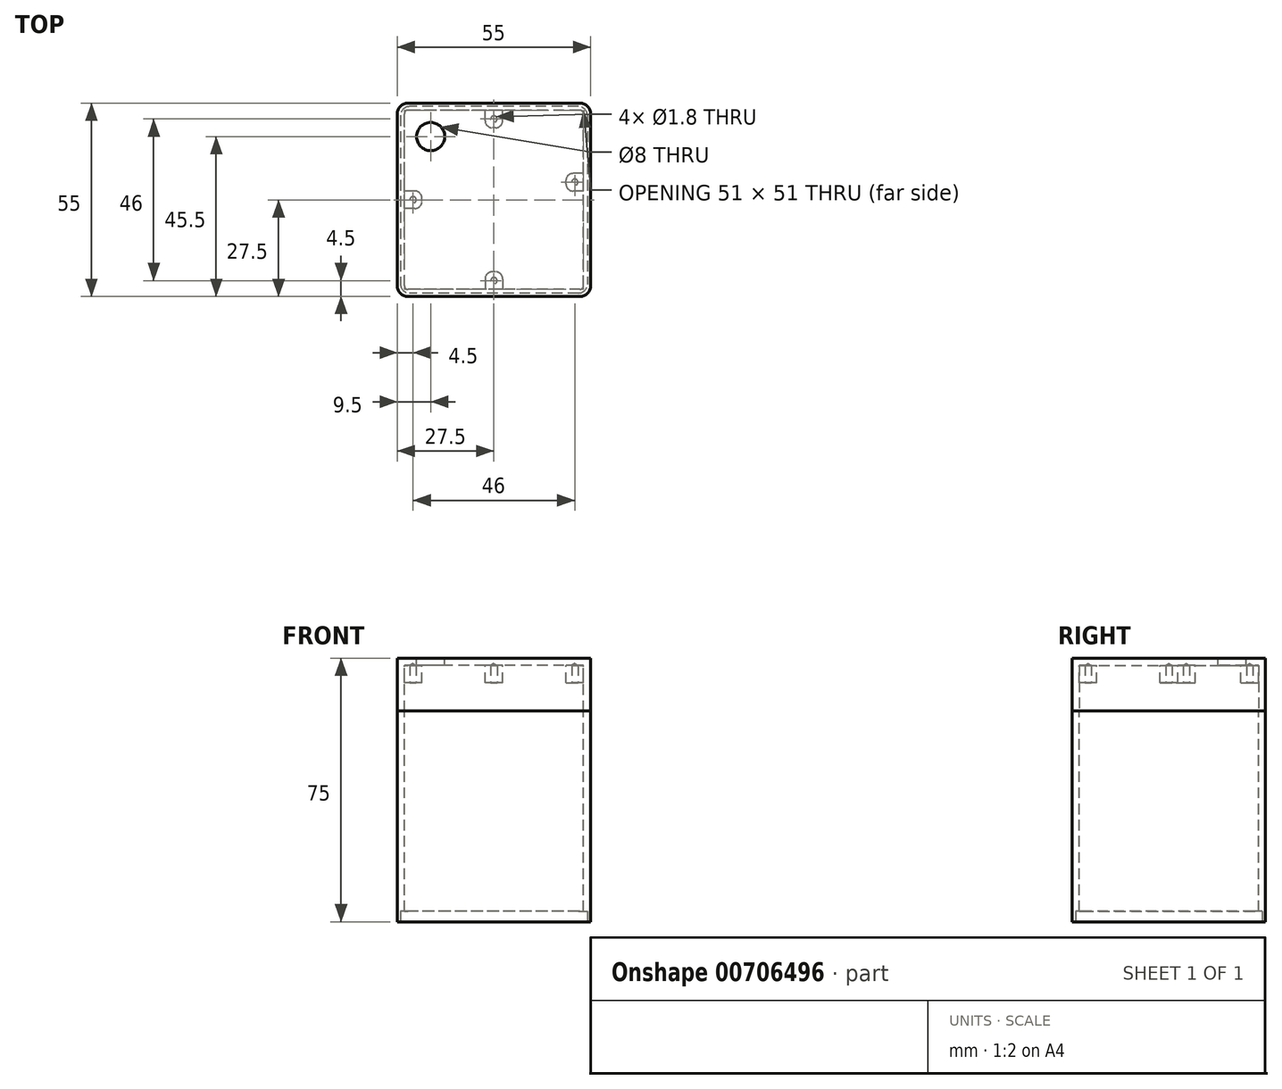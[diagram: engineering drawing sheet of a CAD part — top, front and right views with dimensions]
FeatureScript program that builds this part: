
annotation { "Feature Type Name" : "Feature", "Feature Type Description" : "" }
export const myFeature = defineFeature(function(context is Context, id is Id, definition is map)
    precondition{}
    {
        {
            var Q0;
            Q0=qCreatedBy(makeId("Top.planeOp"),FACE);
            var sketch = newSketch(context, id + "F0", { "sketchPlane" : qUnion([Q0])});
            skLineSegment(sketch, "E0.bottom", {"start": v(27.5, -27.5) * mm, "end": v(-27.5, -27.5) * mm});
            skLineSegment(sketch, "E0.top", {"start": v(27.5, 27.5) * mm, "end": v(-27.5, 27.5) * mm});
            skLineSegment(sketch, "E0.left", {"start": v(27.5, -27.5) * mm, "end": v(27.5, 27.5) * mm});
            skLineSegment(sketch, "E0.right", {"start": v(-27.5, -27.5) * mm, "end": v(-27.5, 27.5) * mm});
            skPoint(sketch, "E0.middle", {"position": v(0, 0) * mm});
            skSolve(sketch);
        }
        {
            var Q0;
            Q0=makeQuery(id+"F0.imprint","IMPRINT",FACE,{"disambiguationData":[TD([[makeQuery(id+"F0.imprint","IMPRINT",EDGE,{"derivedFrom":sQuery(id+"F0.wireOp",EDGE,"E0.bottom")}),-1.0]])]});
            extrude(context, id + "F1", {"entities" : qUnion([Q0]), "depth" : 15 * mm, "offsetDistance" : 25 * mm});
        }
        {
            var Q0;
            Q0=makeQuery(id+"F1.opExtrude","SWEPT_EDGE",EDGE,{"disambiguationData":[OSD([sQuery(id+"F0.wireOp",EDGE,"E0.top"),sQuery(id+"F0.wireOp",EDGE,"E0.right")])]});
            var Q1;
            Q1=makeQuery(id+"F1.opExtrude","SWEPT_EDGE",EDGE,{"disambiguationData":[OSD([sQuery(id+"F0.wireOp",EDGE,"E0.bottom"),sQuery(id+"F0.wireOp",EDGE,"E0.right")])]});
            var Q2;
            Q2=makeQuery(id+"F1.opExtrude","SWEPT_EDGE",EDGE,{"disambiguationData":[OSD([sQuery(id+"F0.wireOp",EDGE,"E0.bottom"),sQuery(id+"F0.wireOp",EDGE,"E0.left")])]});
            var Q3;
            Q3=makeQuery(id+"F1.opExtrude","SWEPT_EDGE",EDGE,{"disambiguationData":[OSD([sQuery(id+"F0.wireOp",EDGE,"E0.top"),sQuery(id+"F0.wireOp",EDGE,"E0.left")])]});
            fillet(context, id + "F2", {"entities" : qUnion([Q0, Q1, Q2, Q3]), "radius" : 3 * mm, "tangentPropagation" : true, "allowEdgeOverflow" : false});
        }
        {
            var Q0;
            Q0=makeQuery(id+"F1.opExtrude","CAP_FACE",FACE,{"disambiguationData":[OSD([sQuery(id+"F0.wireOp",EDGE,"E0.bottom"),sQuery(id+"F0.wireOp",EDGE,"E0.top"),sQuery(id+"F0.wireOp",EDGE,"E0.left"),sQuery(id+"F0.wireOp",EDGE,"E0.right")])],"isStart":true});
            shell(context, id + "F3", {"entities" : qUnion([Q0]), "thickness" : 2 * mm});
        }
        {
            var Q0;
            Q0=makeQuery(id+"F1.opExtrude","CAP_FACE",FACE,{"disambiguationData":[OSD([sQuery(id+"F0.wireOp",EDGE,"E0.bottom"),sQuery(id+"F0.wireOp",EDGE,"E0.top"),sQuery(id+"F0.wireOp",EDGE,"E0.left"),sQuery(id+"F0.wireOp",EDGE,"E0.right")])],"isStart":false});
            var sketch = newSketch(context, id + "F4", { "sketchPlane" : qUnion([Q0])});
            skCircle(sketch, "E1", {"center": v(-18, 18) * mm, "radius": 4 * mm});
            skLineSegment(sketch, "E2", {"start": v(-18, 18) * mm, "end": v(-18, 32.81) * mm, "construction": true});
            skSolve(sketch);
        }
        {
            var Q0;
            Q0=makeQuery(id+"F4.imprint","IMPRINT",FACE,{"disambiguationData":[TD([[makeQuery(id+"F4.imprint","IMPRINT",EDGE,{"derivedFrom":sQuery(id+"F4.wireOp",EDGE,"E1")}),1.0]])]});
            extrude(context, id + "F5", {"entities" : qUnion([Q0]), "operationType" : NewBodyOperationType.REMOVE, "oppositeDirection" : true, "depth" : 25 * mm, "offsetDistance" : 25 * mm});
        }
        {
            var Q0;
            Q0=makeQuery(id+"F1.opExtrude","CAP_FACE",FACE,{"disambiguationData":[OSD([sQuery(id+"F0.wireOp",EDGE,"E0.bottom"),sQuery(id+"F0.wireOp",EDGE,"E0.top"),sQuery(id+"F0.wireOp",EDGE,"E0.left"),sQuery(id+"F0.wireOp",EDGE,"E0.right")])],"isStart":true});
            extrude(context, id + "F6", {"entities" : qUnion([Q0]), "depth" : 60 * mm, "offsetDistance" : 25 * mm});
        }
        {
            var Q0;
            Q0=makeQuery(id+"F6.opExtrude","CAP_FACE",FACE,{"disambiguationData":[OSD([sQuery(id+"F0.wireOp",EDGE,"E0.bottom"),sQuery(id+"F0.wireOp",EDGE,"E0.top"),sQuery(id+"F0.wireOp",EDGE,"E0.left"),sQuery(id+"F0.wireOp",EDGE,"E0.right")])],"isStart":false});
            var sketch = newSketch(context, id + "F7", { "sketchPlane" : qUnion([Q0])});
            skLineSegment(sketch, "E3.bottom", {"start": v(24.05, -26.55) * mm, "end": v(-24.05, -26.55) * mm});
            skLineSegment(sketch, "E3.top", {"start": v(24.05, 26.55) * mm, "end": v(-24.05, 26.55) * mm});
            skLineSegment(sketch, "E3.left", {"start": v(26.55, -24.05) * mm, "end": v(26.55, 24.05) * mm});
            skLineSegment(sketch, "E3.right", {"start": v(-26.55, -24.05) * mm, "end": v(-26.55, 24.05) * mm});
            skPoint(sketch, "E3.middle", {"position": v(0, 0) * mm});
            skPoint(sketch, "E4.visualSharp", {"position": v(-26.55, -26.55) * mm});
            skArc(sketch, "E4.filletArc", {"start": v(-26.55, -24.05) * mm, "mid": v(-25.82, -25.82) * mm, "end": v(-24.05, -26.55) * mm});
            skPoint(sketch, "E5.visualSharp", {"position": v(26.55, -26.55) * mm});
            skArc(sketch, "E5.filletArc", {"start": v(24.05, -26.55) * mm, "mid": v(25.82, -25.82) * mm, "end": v(26.55, -24.05) * mm});
            skPoint(sketch, "E6.visualSharp", {"position": v(26.55, 26.55) * mm});
            skArc(sketch, "E6.filletArc", {"start": v(26.55, 24.05) * mm, "mid": v(25.82, 25.82) * mm, "end": v(24.05, 26.55) * mm});
            skPoint(sketch, "E7.visualSharp", {"position": v(-26.55, 26.55) * mm});
            skArc(sketch, "E7.filletArc", {"start": v(-24.05, 26.55) * mm, "mid": v(-25.82, 25.82) * mm, "end": v(-26.55, 24.05) * mm});
            skSolve(sketch);
        }
        {
            var Q0;
            Q0 = qSketchRegion(id + "F7", true);
            extrude(context, id + "F8", {"entities" : qUnion([Q0]), "operationType" : NewBodyOperationType.REMOVE, "oppositeDirection" : true, "depth" : 3 * mm, "offsetDistance" : 25 * mm});
        }
        {
            var Q0;
            Q0=makeQuery(id+"F3.opShell","OFFSET_FACE",FACE,{"disambiguationData":[OSD([sQuery(id+"F0.wireOp",EDGE,"E0.bottom"),sQuery(id+"F0.wireOp",EDGE,"E0.top"),sQuery(id+"F0.wireOp",EDGE,"E0.left"),sQuery(id+"F0.wireOp",EDGE,"E0.right")])]});
            var sketch = newSketch(context, id + "F9", { "sketchPlane" : qUnion([Q0])});
            skLineSegment(sketch, "E8.bottom", {"start": v(-20.5, 2.5) * mm, "end": v(-25.5, 2.5) * mm});
            skLineSegment(sketch, "E8.top", {"start": v(-20.5, -2.5) * mm, "end": v(-25.5, -2.5) * mm});
            skLineSegment(sketch, "E8.left", {"start": v(-20.5, 2.5) * mm, "end": v(-20.5, -2.5) * mm});
            skLineSegment(sketch, "E8.right", {"start": v(-25.5, 2.5) * mm, "end": v(-25.5, -2.5) * mm});
            skPoint(sketch, "E8.middle", {"position": v(-23, 0) * mm});
            skLineSegment(sketch, "E9.bottom", {"start": v(2.5, -20.5) * mm, "end": v(-2.5, -20.5) * mm});
            skLineSegment(sketch, "E9.top", {"start": v(2.5, -25.5) * mm, "end": v(-2.5, -25.5) * mm});
            skLineSegment(sketch, "E9.left", {"start": v(2.5, -20.5) * mm, "end": v(2.5, -25.5) * mm});
            skLineSegment(sketch, "E9.right", {"start": v(-2.5, -20.5) * mm, "end": v(-2.5, -25.5) * mm});
            skPoint(sketch, "E9.middle", {"position": v(0, -23) * mm});
            skLineSegment(sketch, "E10.MirrorCS", {"start": v(2.5, 25.5) * mm, "end": v(-2.5, 25.5) * mm});
            skLineSegment(sketch, "E11.MirrorCS", {"start": v(-2.5, 20.5) * mm, "end": v(-2.5, 25.5) * mm});
            skLineSegment(sketch, "E12.MirrorCS", {"start": v(2.5, 20.5) * mm, "end": v(-2.5, 20.5) * mm});
            skPoint(sketch, "E13.MirrorP", {"position": v(0, 23) * mm});
            skLineSegment(sketch, "E14.MirrorCS", {"start": v(2.5, 20.5) * mm, "end": v(2.5, 25.5) * mm});
            skLineSegment(sketch, "E15.bottom", {"start": v(25.5, -2.5) * mm, "end": v(20.5, -2.5) * mm});
            skLineSegment(sketch, "E15.top", {"start": v(25.5, -7.5) * mm, "end": v(20.5, -7.5) * mm});
            skLineSegment(sketch, "E15.left", {"start": v(25.5, -2.5) * mm, "end": v(25.5, -7.5) * mm});
            skLineSegment(sketch, "E15.right", {"start": v(20.5, -2.5) * mm, "end": v(20.5, -7.5) * mm});
            skPoint(sketch, "E15.middle", {"position": v(23, -5) * mm});
            skSolve(sketch);
        }
        {
            var Q0;
            Q0=makeQuery(id+"F9.imprint","IMPRINT",FACE,{"disambiguationData":[TD([[makeQuery(id+"F9.imprint","IMPRINT",EDGE,{"derivedFrom":sQuery(id+"F9.wireOp",EDGE,"E8.bottom")}),1.0]])]});
            var Q1;
            Q1=makeQuery(id+"F9.imprint","IMPRINT",FACE,{"disambiguationData":[TD([[makeQuery(id+"F9.imprint","IMPRINT",EDGE,{"derivedFrom":sQuery(id+"F9.wireOp",EDGE,"E9.bottom")}),1.0]])]});
            var Q2;
            Q2=makeQuery(id+"F9.imprint","IMPRINT",FACE,{"disambiguationData":[TD([[makeQuery(id+"F9.imprint","IMPRINT",EDGE,{"derivedFrom":sQuery(id+"F9.wireOp",EDGE,"lUhLYoH8-ef4B-Amfr-58X2-60gpwSc5HfLL.bottom")}),1.0]])]});
            var Q3;
            Q3=makeQuery(id+"F9.imprint","IMPRINT",FACE,{"disambiguationData":[TD([[makeQuery(id+"F9.imprint","IMPRINT",EDGE,{"derivedFrom":sQuery(id+"F9.wireOp",EDGE,"c64a179b-c89c-4805-b942-4bc86fe0bf4f0.MirrorCS")}),-1.0]])]});
            var Q4;
            Q4=makeQuery(id+"F9.imprint","IMPRINT",FACE,{"disambiguationData":[TD([[makeQuery(id+"F9.imprint","IMPRINT",EDGE,{"derivedFrom":sQuery(id+"F9.wireOp",EDGE,"E10.MirrorCS")}),1.0]])]});
            var Q5;
            Q5=makeQuery(id+"F9.imprint","IMPRINT",FACE,{"disambiguationData":[TD([[makeQuery(id+"F9.imprint","IMPRINT",EDGE,{"derivedFrom":sQuery(id+"F9.wireOp",EDGE,"E15.bottom")}),1.0]])]});
            extrude(context, id + "F10", {"entities" : qUnion([Q0, Q1, Q2, Q3, Q4, Q5]), "operationType" : NewBodyOperationType.ADD, "depth" : 5 * mm, "offsetDistance" : 25 * mm});
        }
        {
            var Q0;
            Q0=makeQuery(id+"F10.opExtrude","SWEPT_EDGE",EDGE,{"disambiguationData":[OSD([sQuery(id+"F9.wireOp",EDGE,"E8.top"),sQuery(id+"F9.wireOp",EDGE,"E8.left")])]});
            var Q1;
            Q1=makeQuery(id+"F10.opExtrude","SWEPT_EDGE",EDGE,{"disambiguationData":[OSD([sQuery(id+"F9.wireOp",EDGE,"E8.bottom"),sQuery(id+"F9.wireOp",EDGE,"E8.left")])]});
            var Q2;
            Q2=makeQuery(id+"F10.opExtrude","SWEPT_EDGE",EDGE,{"disambiguationData":[OSD([sQuery(id+"F9.wireOp",EDGE,"lUhLYoH8-ef4B-Amfr-58X2-60gpwSc5HfLL.top"),sQuery(id+"F9.wireOp",EDGE,"lUhLYoH8-ef4B-Amfr-58X2-60gpwSc5HfLL.left")])]});
            var Q3;
            Q3=makeQuery(id+"F10.opExtrude","SWEPT_EDGE",EDGE,{"disambiguationData":[OSD([sQuery(id+"F9.wireOp",EDGE,"lUhLYoH8-ef4B-Amfr-58X2-60gpwSc5HfLL.top"),sQuery(id+"F9.wireOp",EDGE,"lUhLYoH8-ef4B-Amfr-58X2-60gpwSc5HfLL.right")])]});
            var Q4;
            Q4=makeQuery(id+"F10.opExtrude","SWEPT_EDGE",EDGE,{"disambiguationData":[OSD([sQuery(id+"F9.wireOp",EDGE,"E9.bottom"),sQuery(id+"F9.wireOp",EDGE,"E9.left")])]});
            var Q5;
            Q5=makeQuery(id+"F10.opExtrude","SWEPT_EDGE",EDGE,{"disambiguationData":[OSD([sQuery(id+"F9.wireOp",EDGE,"E9.bottom"),sQuery(id+"F9.wireOp",EDGE,"E9.right")])]});
            var Q6;
            Q6=makeQuery(id+"F10.opExtrude","SWEPT_EDGE",EDGE,{"disambiguationData":[OSD([sQuery(id+"F9.wireOp",EDGE,"c64a179b-c89c-4805-b942-4bc86fe0bf4f1.MirrorCS"),sQuery(id+"F9.wireOp",EDGE,"c64a179b-c89c-4805-b942-4bc86fe0bf4f4.MirrorCS")])]});
            var Q7;
            Q7=makeQuery(id+"F10.opExtrude","SWEPT_EDGE",EDGE,{"disambiguationData":[OSD([sQuery(id+"F9.wireOp",EDGE,"c64a179b-c89c-4805-b942-4bc86fe0bf4f2.MirrorCS"),sQuery(id+"F9.wireOp",EDGE,"c64a179b-c89c-4805-b942-4bc86fe0bf4f4.MirrorCS")])]});
            var Q8;
            Q8=makeQuery(id+"F10.opExtrude","SWEPT_EDGE",EDGE,{"disambiguationData":[OSD([sQuery(id+"F9.wireOp",EDGE,"E11.MirrorCS"),sQuery(id+"F9.wireOp",EDGE,"E12.MirrorCS")])]});
            var Q9;
            Q9=makeQuery(id+"F10.opExtrude","SWEPT_EDGE",EDGE,{"disambiguationData":[OSD([sQuery(id+"F9.wireOp",EDGE,"E12.MirrorCS"),sQuery(id+"F9.wireOp",EDGE,"E14.MirrorCS")])]});
            var Q10;
            Q10=makeQuery(id+"F10.opExtrude","SWEPT_EDGE",EDGE,{"disambiguationData":[OSD([sQuery(id+"F9.wireOp",EDGE,"E15.bottom"),sQuery(id+"F9.wireOp",EDGE,"E15.right")])]});
            var Q11;
            Q11=makeQuery(id+"F10.opExtrude","SWEPT_EDGE",EDGE,{"disambiguationData":[OSD([sQuery(id+"F9.wireOp",EDGE,"E15.top"),sQuery(id+"F9.wireOp",EDGE,"E15.right")])]});
            fillet(context, id + "F11", {"entities" : qUnion([Q0, Q1, Q2, Q3, Q4, Q5, Q6, Q7, Q8, Q9, Q10, Q11]), "radius" : 2 * mm, "tangentPropagation" : true, "allowEdgeOverflow" : false});
        }
        {
            var Q0;
            Q0=makeQuery(id+"F10.opExtrude","CAP_FACE",FACE,{"disambiguationData":[OSD([sQuery(id+"F9.wireOp",EDGE,"E8.bottom"),sQuery(id+"F9.wireOp",EDGE,"E8.top"),sQuery(id+"F9.wireOp",EDGE,"E8.left"),sQuery(id+"F9.wireOp",EDGE,"E8.right")])],"isStart":false});
            var sketch = newSketch(context, id + "F12", { "sketchPlane" : qUnion([Q0])});
            skPoint(sketch, "E16", {"position": v(-23, 0) * mm});
            skPoint(sketch, "E17", {"position": v(0, -23) * mm});
            skPoint(sketch, "E18.MirrorP", {"position": v(0, 23) * mm});
            skPoint(sketch, "E19", {"position": v(23, -5) * mm});
            skSolve(sketch);
        }
        {
            var Q0;
            Q0=sQuery(id+"F12.wireOp",VERTEX,"E19");
            var Q1;
            Q1=sQuery(id+"F12.wireOp",VERTEX,"E17");
            var Q2;
            Q2=sQuery(id+"F12.wireOp",VERTEX,"E18.MirrorP");
            var Q3;
            Q3=sQuery(id+"F12.wireOp",VERTEX,"E16");
            var Q4;
            Q4=makeQuery(id+"F1.opExtrude","SWEPT_BODY",BODY,{"disambiguationData":[OSD([sQuery(id+"F0.wireOp",EDGE,"E0.bottom"),sQuery(id+"F0.wireOp",EDGE,"E0.top"),sQuery(id+"F0.wireOp",EDGE,"E0.left"),sQuery(id+"F0.wireOp",EDGE,"E0.right")])]});
            hole(context, id + "F13", {"style" : HoleStyle.SIMPLE, "endStyle" : HoleEndStyle.BLIND, "holeDiameter" : 1.8 * mm, "majorDiameter" : 5 * mm, "holeDepth" : 5 * mm, "isTappedThrough" : true, "tappedDepth" : 6 * mm, "tapClearance" : 3, "locations" : qUnion([Q0, Q1, Q2, Q3]), "scope" : qUnion([Q4])});
        }
    });
